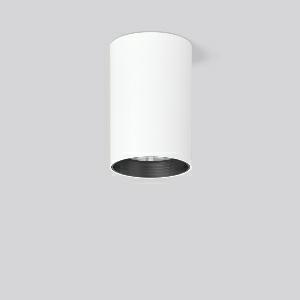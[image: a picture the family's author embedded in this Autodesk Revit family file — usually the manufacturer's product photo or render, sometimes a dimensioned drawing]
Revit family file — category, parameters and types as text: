
# Revit family: heledon_maxi_a_931220_002_2_0c8e
name_source: partatom
category: Lighting Fixtures
units: mm (PartAtom-declared; Revit-internal decimal feet)

## family parameters
Cut with Voids When Loaded = No
Host = Face
Light Source = No
Part Type = Normal
Room Calculation Point = No
Round Connector Dimension = Use Diameter
Shared = No

## types (1)
- HELEDON maxi A (1 x LED Modul 927, 2650 lm, 2700)
    Apparent Load = 25 VA
    Approval mark = CE
    CIE Flux Codes = 97 100 100 100 100
    Color Rendering = 92
    Color Temperature = 2700
    Default Elevation = 1800 mm
    Description = Series: HELEDON maxi
Cylindrical surface-mounted downlight. Housing: die-cast aluminium, powder-coated. Internal ceiling frame polycarbonate with bayonet mounting. Black plastic ring and recessed LED to prevent glare from the side. Optical assembly with lens made of plastic (polycarbonate) for the best homogeneous light distribution - can be changed without tools. Best colour rendering index Ra>90. Suitable for Ceiling mounting. Easy installation with a separate ceiling frame with bayonet mounting and plug connection. Driver integrated. Connected via plug-in connector. High quality converter without flickering and stroboscopic effect. The following accessories can be mounted without use of tools: interchangeable lenses, decorative glasses, honeycomb louvre, clear and frosted diffusers, white interchangeable plastic ring. 
Colour: traffic white, matt (RAL 9016)
Diameter: 123 mm
Height: 183 mm
Lamp: LED
Socket: without socket
Colour temperature: 2700K
Colour rendering index (CRI): 92
System power: 25 W
Rated luminous flux: 2650 lm
Luminous efficiency: 106 lm/W
Control gear: Regulated power supply
Protection class: I
Type of protection: IP 20
    Height = 183 mm
    Lamp = 1 x LED Modul 927
    Lamp Light Flux = 2650 lm
    Lamp count = 1
    Length = 123 mm
    Lifetime = 50000 h
    Luminous efficacy = 106 lm/W
    Manufacturer = RZB
    ModVariant = No
    Model = 931220.002.2
    Mounting Place = Ceiling
    Mounting Type = Surface mounted
    Number of Poles = 1
    OnlyDefault = Yes
    Power Factor = 1
    Product Name = HELEDON maxi A
    Product group = Surface mounted downlights
    ProductGroupID = 302
    Protection Class = Protection class I
    Protection Degree = IP 20
    RLX_Detail_Level = 1
    RLX_Emergency_Light_Flux = 0 lm
    RLX_Emergency_Type = 0
    RLX_Emergency_Type_DB = No
    RlxData = <blob elided: 97449 chars, md5=3c2909a9>
    Socket = socket
    Standby Power = 0 W
    System Light Flux = 2650 lm
    System Power = 25 W
    Type Comments = Product without accessories
    Type Image = 931193.002.jpg
    URL = http://relux.com
    VarID = ---
    Voltage = 230 V
    Voltage Range = 220-240 V
    Weight = 0.00 kg
    Width = 0 mm  [stored 0 ft]

note: [stored X ft] marks values corroborated as IEEE doubles in the binary element streams (Revit-internal decimal feet)

## geometry (parser evidence)
native form markers: Blend x4, Sweep x10
no freeform markers — native parametric forms only
